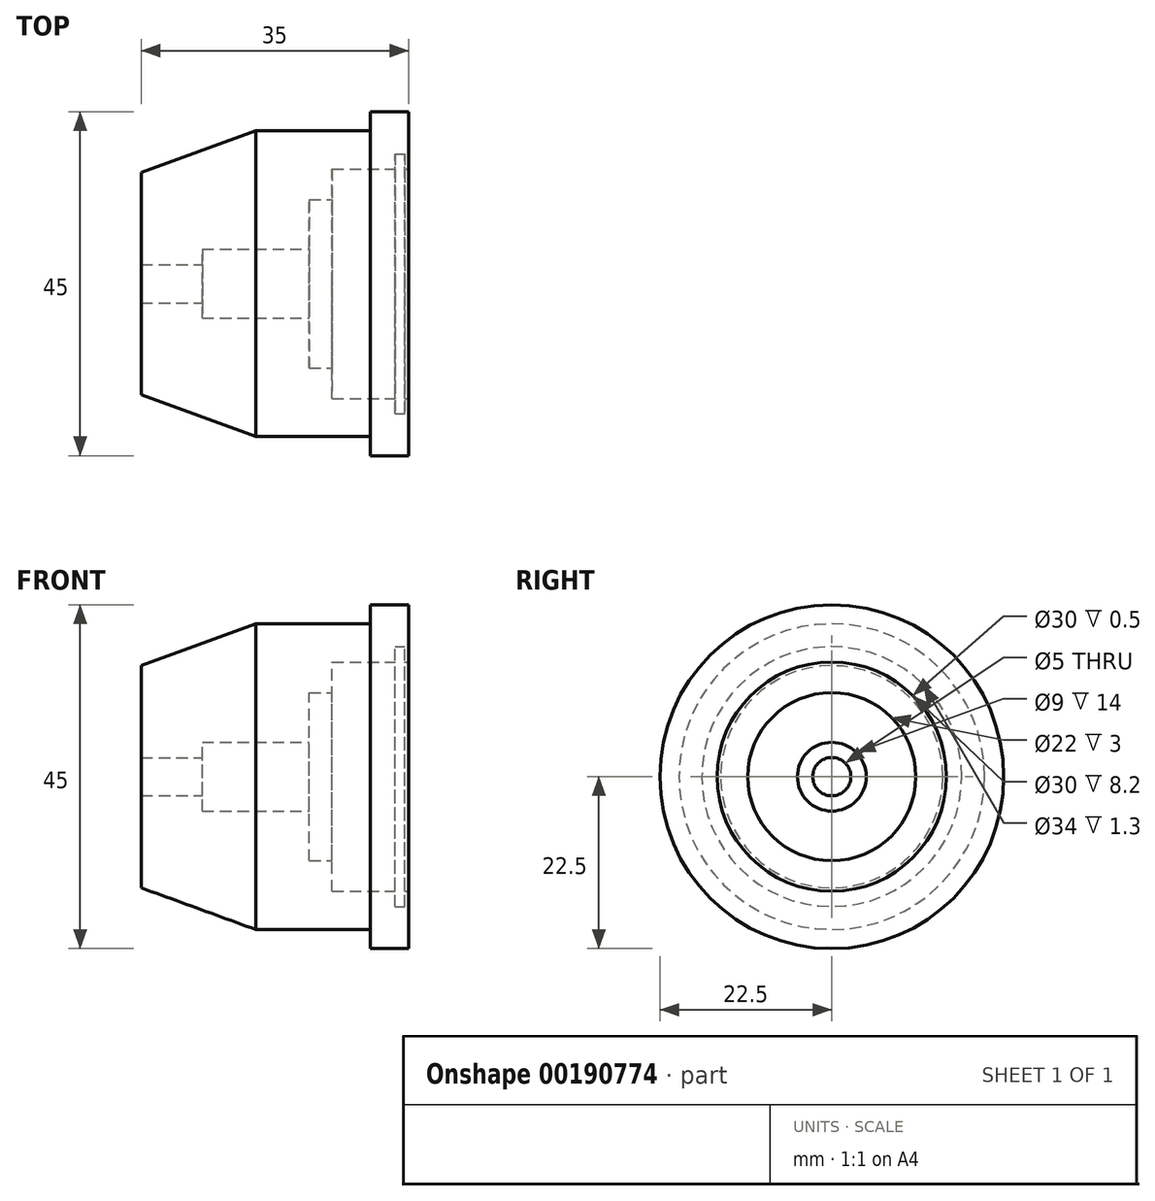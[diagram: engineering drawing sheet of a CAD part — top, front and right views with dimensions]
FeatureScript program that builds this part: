
annotation { "Feature Type Name" : "Feature", "Feature Type Description" : "" }
export const myFeature = defineFeature(function(context is Context, id is Id, definition is map)
    precondition{}
    {
        {
            var Q0;
            Q0=qCreatedBy(makeId("Front.planeOp"),FACE);
            var sketch = newSketch(context, id + "F0", { "sketchPlane" : qUnion([Q0])});
            skLineSegment(sketch, "E0", {"start": v(0, 0) * mm, "end": v(-20.47, 0) * mm, "construction": true});
            skLineSegment(sketch, "E1", {"start": v(0, 0) * mm, "end": v(0, 22.5) * mm});
            skLineSegment(sketch, "E2", {"start": v(0, 22.5) * mm, "end": v(-5, 22.5) * mm});
            skLineSegment(sketch, "E3", {"start": v(-5, 20) * mm, "end": v(-5, 22.5) * mm});
            skLineSegment(sketch, "E4", {"start": v(-5, 20) * mm, "end": v(-20, 20) * mm});
            skLineSegment(sketch, "E5", {"start": v(-35, 14.54) * mm, "end": v(-35, 2.5) * mm});
            skLineSegment(sketch, "E6", {"start": v(-35, 2.5) * mm, "end": v(-27, 2.5) * mm});
            skLineSegment(sketch, "E7", {"start": v(-13, 4.5) * mm, "end": v(-13, 11) * mm});
            skLineSegment(sketch, "E8", {"start": v(-13, 11) * mm, "end": v(-10, 11) * mm});
            skLineSegment(sketch, "E9", {"start": v(-10, 15) * mm, "end": v(-10, 11) * mm});
            skLineSegment(sketch, "E10", {"start": v(-10, 15) * mm, "end": v(-1.8, 15) * mm});
            skLineSegment(sketch, "E11", {"start": v(-13, 4.5) * mm, "end": v(-27, 4.5) * mm});
            skLineSegment(sketch, "E12", {"start": v(-27, 4.5) * mm, "end": v(-27, 2.5) * mm});
            skLineSegment(sketch, "E13", {"start": v(-20, 20) * mm, "end": v(-35, 14.54) * mm});
            skLineSegment(sketch, "E14.top", {"start": v(-0.5, 17) * mm, "end": v(-1.8, 17) * mm});
            skLineSegment(sketch, "E14.left", {"start": v(-0.5, 15) * mm, "end": v(-0.5, 17) * mm});
            skLineSegment(sketch, "E14.right", {"start": v(-1.8, 15) * mm, "end": v(-1.8, 17) * mm});
            skLineSegment(sketch, "E15.trimOffspring", {"start": v(-0.5, 15) * mm, "end": v(0, 15) * mm});
            skSolve(sketch);
        }
        {
            var Q0;
            {var subQ1=sQuery(id+"F0.wireOp",EDGE,"E2");Q0=makeQuery(id+"F0.imprint","IMPRINT",FACE,{"disambiguationData":[TD([[makeQuery(id+"F0.imprint","IMPRINT",EDGE,{"derivedFrom":subQ1}),1.0]])]});}
            var Q1;
            Q1=sQuery(id+"F0.wireOp",EDGE,"E0");
            revolve(context, id + "F1", {"entities" : qUnion([Q0]), "axis" : qUnion([Q1]), "revolveType" : RevolveType.FULL});
        }
    });
